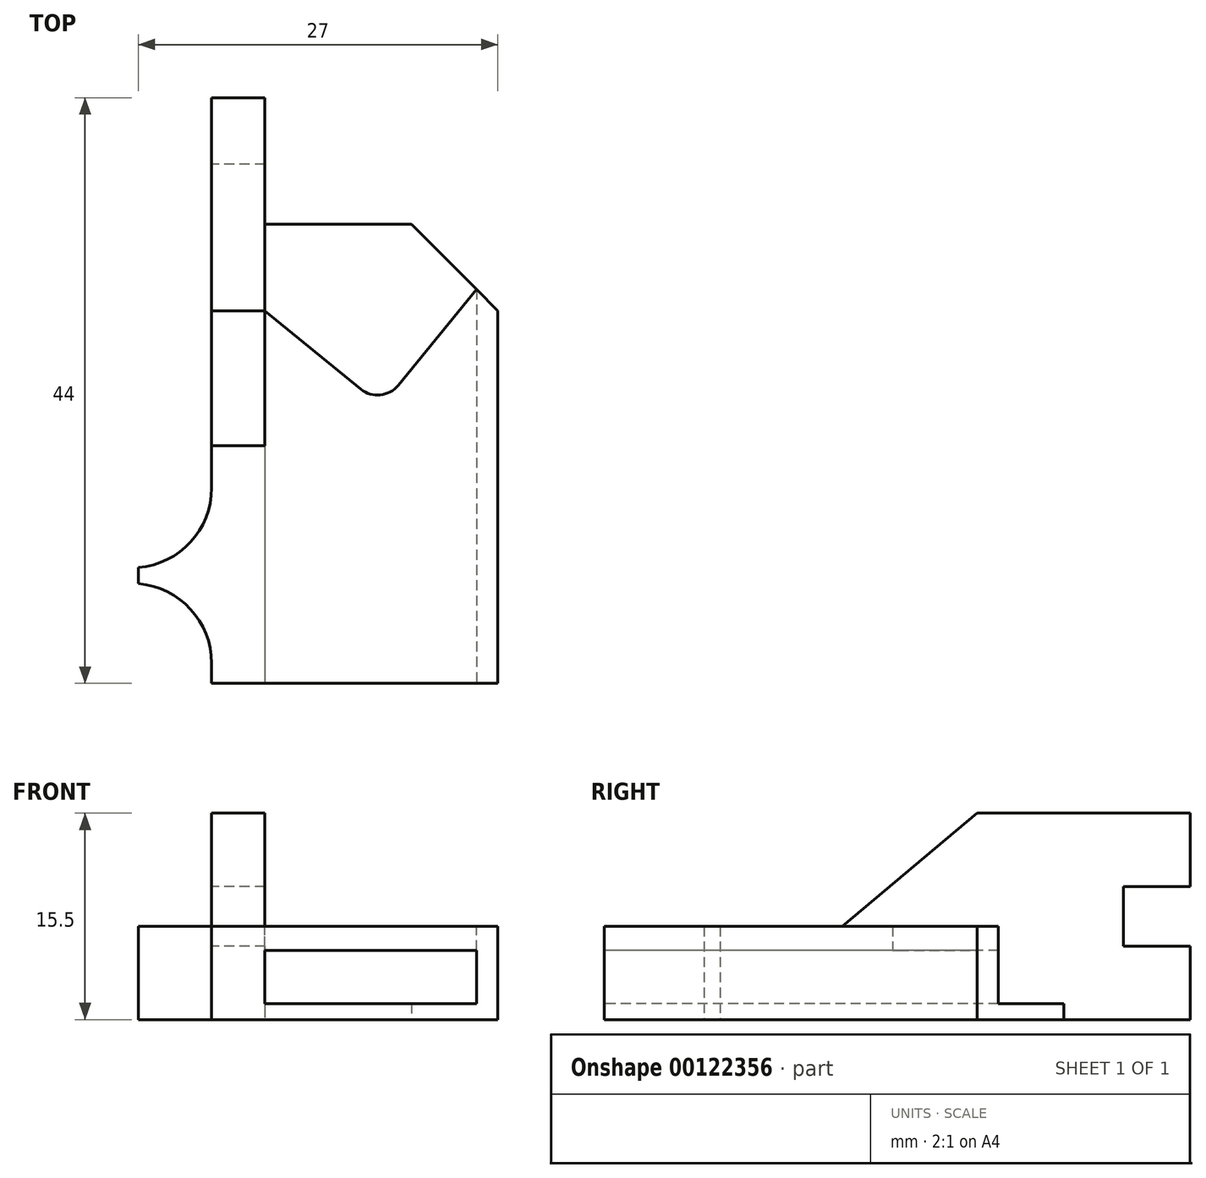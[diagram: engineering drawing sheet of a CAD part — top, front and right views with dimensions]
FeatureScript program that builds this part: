
annotation { "Feature Type Name" : "Feature", "Feature Type Description" : "" }
export const myFeature = defineFeature(function(context is Context, id is Id, definition is map)
    precondition{}
    {
        {
            var Q0;
            Q0=qCreatedBy(makeId("Top.planeOp"),FACE);
            var sketch = newSketch(context, id + "F0", { "sketchPlane" : qUnion([Q0])});
            skLineSegment(sketch, "E0", {"start": v(-16.28, -17.54) * mm, "end": v(-16.28, -10.04) * mm});
            skLineSegment(sketch, "E1", {"start": v(-16.28, -10.04) * mm, "end": v(-21.78, -10.04) * mm});
            skLineSegment(sketch, "E2", {"start": v(-21.78, -8.84) * mm, "end": v(-16.28, -8.84) * mm});
            skLineSegment(sketch, "E3", {"start": v(-16.28, -8.84) * mm, "end": v(-16.28, 16.96) * mm});
            skLineSegment(sketch, "E4", {"start": v(-16.28, 16.96) * mm, "end": v(-1.28, 16.96) * mm});
            skLineSegment(sketch, "E5", {"start": v(-1.28, 16.96) * mm, "end": v(5.22, 10.46) * mm});
            skLineSegment(sketch, "E6", {"start": v(5.22, 10.46) * mm, "end": v(5.22, -17.54) * mm});
            skLineSegment(sketch, "E7", {"start": v(5.22, -17.54) * mm, "end": v(-16.28, -17.54) * mm});
            skLineSegment(sketch, "E8", {"start": v(-21.78, -10.04) * mm, "end": v(-21.78, -8.84) * mm});
            skSolve(sketch);
        }
        {
            var Q0;
            Q0=makeQuery(id+"F0.imprint","IMPRINT",FACE,{"disambiguationData":[TD([[makeQuery(id+"F0.imprint","IMPRINT",EDGE,{"derivedFrom":sQuery(id+"F0.wireOp",EDGE,"E0")}),-1.0]])]});
            extrude(context, id + "F1", {"entities" : qUnion([Q0]), "depth" : 7 * mm});
        }
        {
            var Q0;
            Q0=makeQuery(id+"F1.opExtrude","SWEPT_EDGE",EDGE,{"disambiguationData":[OSD([sQuery(id+"F0.wireOp",EDGE,"E0"),sQuery(id+"F0.wireOp",EDGE,"E1")])]});
            var Q1;
            Q1=makeQuery(id+"F1.opExtrude","SWEPT_EDGE",EDGE,{"disambiguationData":[OSD([sQuery(id+"F0.wireOp",EDGE,"E2"),sQuery(id+"F0.wireOp",EDGE,"E3")])]});
            fillet(context, id + "F2", {"entities" : qUnion([Q0, Q1]), "radius" : 6 * mm, "tangentPropagation" : true, "allowEdgeOverflow" : false});
        }
        {
            var Q0;
            Q0=makeQuery(id+"F1.opExtrude","SWEPT_FACE",FACE,{"disambiguationData":[OSD([sQuery(id+"F0.wireOp",EDGE,"E7")])]});
            var sketch = newSketch(context, id + "F3", { "sketchPlane" : qUnion([Q0])});
            skLineSegment(sketch, "E9.bottom", {"start": v(-12.28, 5.2) * mm, "end": v(3.62, 5.2) * mm});
            skLineSegment(sketch, "E9.top", {"start": v(-12.28, 1.2) * mm, "end": v(3.62, 1.2) * mm});
            skLineSegment(sketch, "E9.left", {"start": v(-12.28, 5.2) * mm, "end": v(-12.28, 1.2) * mm});
            skLineSegment(sketch, "E9.right", {"start": v(3.62, 5.2) * mm, "end": v(3.62, 1.2) * mm});
            skSolve(sketch);
        }
        {
            var Q0;
            Q0=makeQuery(id+"F3.imprint","IMPRINT",FACE,{"disambiguationData":[TD([[makeQuery(id+"F3.imprint","IMPRINT",EDGE,{"derivedFrom":sQuery(id+"F3.wireOp",EDGE,"E9.bottom")}),-1.0]])]});
            extrude(context, id + "F4", {"entities" : qUnion([Q0]), "operationType" : NewBodyOperationType.REMOVE, "endBound" : BoundingType.THROUGH_ALL, "oppositeDirection" : true, "depth" : 25 * mm});
        }
        {
            var Q0;
            Q0=qCreatedBy(makeId("Top.planeOp"),FACE);
            var sketch = newSketch(context, id + "F5", { "sketchPlane" : qUnion([Q0])});
            skLineSegment(sketch, "E10.bottom", {"start": v(-12.28, 26.46) * mm, "end": v(-16.28, 26.46) * mm});
            skLineSegment(sketch, "E10.top", {"start": v(-12.28, 10.46) * mm, "end": v(-16.28, 10.46) * mm});
            skLineSegment(sketch, "E10.left", {"start": v(-12.28, 26.46) * mm, "end": v(-12.28, 10.46) * mm});
            skLineSegment(sketch, "E10.right", {"start": v(-16.28, 26.46) * mm, "end": v(-16.28, 10.46) * mm});
            skSolve(sketch);
        }
        {
            var Q0;
            Q0=makeQuery(id+"F5.imprint","IMPRINT",FACE,{"disambiguationData":[TD([[makeQuery(id+"F5.imprint","IMPRINT",EDGE,{"derivedFrom":sQuery(id+"F5.wireOp",EDGE,"E10.bottom")}),1.0]])]});
            extrude(context, id + "F6", {"entities" : qUnion([Q0]), "operationType" : NewBodyOperationType.ADD, "depth" : 15.5 * mm});
        }
        {
            var Q0;
            Q0=makeQuery(id+"F1.opExtrude","CAP_FACE",FACE,{"disambiguationData":[OSD([sQuery(id+"F0.wireOp",EDGE,"E0"),sQuery(id+"F0.wireOp",EDGE,"E1"),sQuery(id+"F0.wireOp",EDGE,"E2"),sQuery(id+"F0.wireOp",EDGE,"E3"),sQuery(id+"F0.wireOp",EDGE,"E4"),sQuery(id+"F0.wireOp",EDGE,"E5"),sQuery(id+"F0.wireOp",EDGE,"E6"),sQuery(id+"F0.wireOp",EDGE,"E7"),sQuery(id+"F0.wireOp",EDGE,"E8")])],"isStart":false});
            var sketch = newSketch(context, id + "F7", { "sketchPlane" : qUnion([Q0])});
            skLineSegment(sketch, "E11", {"start": v(-12.28, 10.46) * mm, "end": v(-3.53, 3.3) * mm});
            skLineSegment(sketch, "E12", {"start": v(-3.53, 3.3) * mm, "end": v(3.62, 12.06) * mm});
            skSolve(sketch);
        }
        {
            var Q0;
            Q0=makeQuery(id+"F7.imprint","IMPRINT",FACE,{"disambiguationData":[TD([[makeQuery(id+"F7.imprint","IMPRINT",EDGE,{"derivedFrom":sQuery(id+"F7.wireOp",EDGE,"E11")}),1.0]])]});
            var Q1;
            Q1=makeQuery(id+"F4.boolean.opBoolean","COPY",FACE,{"derivedFrom":makeQuery(id+"F4.opExtrude","SWEPT_FACE",FACE,{"disambiguationData":[OSD([sQuery(id+"F3.wireOp",EDGE,"E9.top")])]})});
            extrude(context, id + "F8", {"entities" : qUnion([Q0]), "operationType" : NewBodyOperationType.REMOVE, "endBound" : BoundingType.UP_TO_SURFACE, "oppositeDirection" : true, "endBoundEntityFace" : qUnion([Q1]), "depth" : 25 * mm});
        }
        {
            var Q0;
            Q0=makeQuery(id+"F8.boolean.opBoolean","COPY",EDGE,{"derivedFrom":makeQuery(id+"F8.opExtrude","SWEPT_EDGE",EDGE,{"disambiguationData":[OSD([sQuery(id+"F7.wireOp",EDGE,"E11"),sQuery(id+"F7.wireOp",EDGE,"E12")])]})});
            var Q1;
            Q1=makeQuery(id+"F8.boolean.opBoolean","COPY",EDGE,{"derivedFrom":makeQuery(id+"F8.opExtrude","SWEPT_EDGE",EDGE,{"disambiguationData":[OSD([sQuery(id+"F0.wireOp",EDGE,"E5"),sQuery(id+"F7.wireOp",EDGE,"E12")])]})});
            fillet(context, id + "F9", {"entities" : qUnion([Q0, Q1]), "radius" : 2 * mm, "tangentPropagation" : true, "allowEdgeOverflow" : false});
        }
        {
            var Q0;
            Q0=makeQuery(id+"F6.boolean.opBoolean","MERGE",FACE,{"derivedFrom":[makeQuery(id+"F1.opExtrude","SWEPT_FACE",FACE,{"disambiguationData":[OSD([sQuery(id+"F0.wireOp",EDGE,"E3")])]}),makeQuery(id+"F6.opExtrude","SWEPT_FACE",FACE,{"disambiguationData":[OSD([sQuery(id+"F5.wireOp",EDGE,"E10.right")])]})]});
            var sketch = newSketch(context, id + "F10", { "sketchPlane" : qUnion([Q0])});
            skLineSegment(sketch, "E13.bottom", {"start": v(-26.46, 10) * mm, "end": v(-21.46, 10) * mm});
            skLineSegment(sketch, "E13.top", {"start": v(-26.46, 5.5) * mm, "end": v(-21.46, 5.5) * mm});
            skLineSegment(sketch, "E13.left", {"start": v(-26.46, 10) * mm, "end": v(-26.46, 5.5) * mm});
            skLineSegment(sketch, "E13.right", {"start": v(-21.46, 10) * mm, "end": v(-21.46, 5.5) * mm});
            skLineSegment(sketch, "E14", {"start": v(-10.46, 15.5) * mm, "end": v(-0.33, 7) * mm});
            skSolve(sketch);
        }
        {
            var Q0;
            Q0=makeQuery(id+"F10.imprint","IMPRINT",FACE,{"disambiguationData":[TD([[makeQuery(id+"F10.imprint","IMPRINT",EDGE,{"derivedFrom":sQuery(id+"F10.wireOp",EDGE,"E13.bottom")}),-1.0]])]});
            extrude(context, id + "F11", {"entities" : qUnion([Q0]), "operationType" : NewBodyOperationType.REMOVE, "endBound" : BoundingType.UP_TO_NEXT, "oppositeDirection" : true, "depth" : 25 * mm});
        }
        {
            var Q0;
            {var subQ0=sQuery(id+"F10.wireOp",EDGE,"E14");Q0=makeQuery(id+"F10.imprint","IMPRINT",FACE,{"disambiguationData":[TD([[makeQuery(id+"F10.imprint","IMPRINT",EDGE,{"derivedFrom":subQ0}),-1.0]])]});}
            extrude(context, id + "F12", {"entities" : qUnion([Q0]), "operationType" : NewBodyOperationType.ADD, "oppositeDirection" : true, "depth" : 4 * mm});
        }
    });
